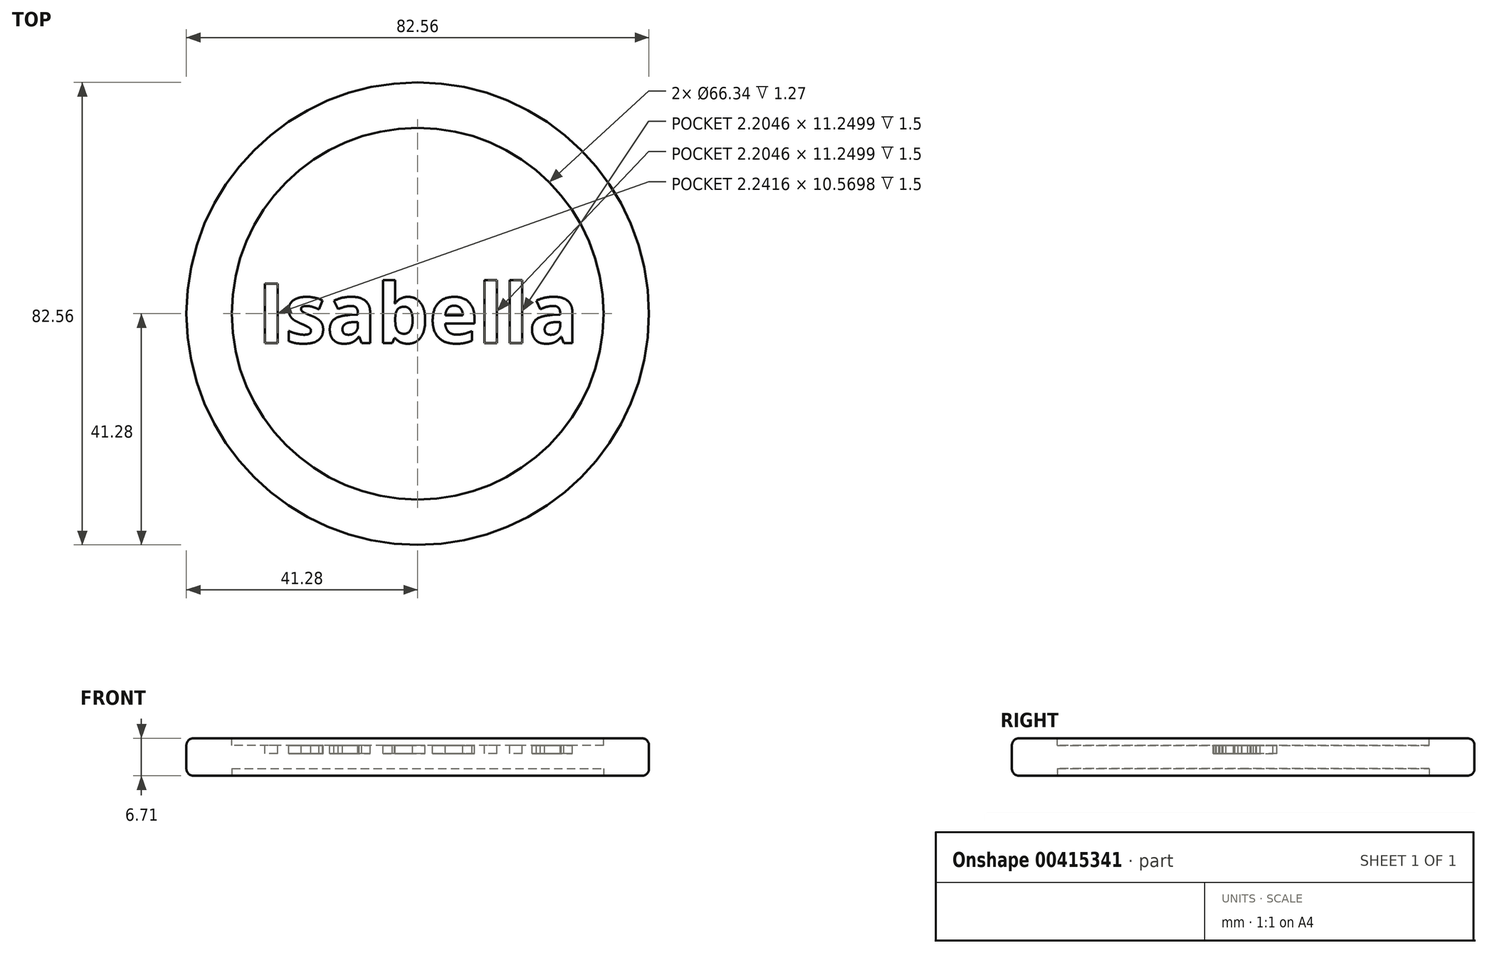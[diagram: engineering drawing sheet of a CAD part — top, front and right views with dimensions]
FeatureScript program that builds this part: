
annotation { "Feature Type Name" : "Feature", "Feature Type Description" : "" }
export const myFeature = defineFeature(function(context is Context, id is Id, definition is map)
    precondition{}
    {
        {
            var Q0;
            Q0=qCreatedBy(makeId("Top.planeOp"),FACE);
            var sketch = newSketch(context, id + "F0", { "sketchPlane" : qUnion([Q0])});
            skCircle(sketch, "E0", {"center": v(0, 0) * mm, "radius": 41.28 * mm});
            skSolve(sketch);
        }
        {
            var Q0;
            Q0=makeQuery(id+"F0.imprint","IMPRINT",FACE,{"disambiguationData":[TD([[makeQuery(id+"F0.imprint","IMPRINT",EDGE,{"derivedFrom":sQuery(id+"F0.wireOp",EDGE,"E0")}),1.0]])]});
            extrude(context, id + "F1", {"entities" : qUnion([Q0]), "depth" : 6.7 * mm});
        }
        {
            var Q0;
            Q0=makeQuery(id+"F1.opExtrude","CAP_FACE",FACE,{"disambiguationData":[OSD([sQuery(id+"F0.wireOp",EDGE,"E0")])],"isStart":false});
            var sketch = newSketch(context, id + "F2", { "sketchPlane" : qUnion([Q0])});
            skCircle(sketch, "E1.0", {"center": v(0, 0) * mm, "radius": 33.17 * mm});
            skSolve(sketch);
        }
        {
            var Q0;
            Q0=makeQuery(id+"F2.imprint","IMPRINT",FACE,{"disambiguationData":[TD([[makeQuery(id+"F2.imprint","IMPRINT",EDGE,{"derivedFrom":sQuery(id+"F2.wireOp",EDGE,"E1.0")}),1.0]])]});
            extrude(context, id + "F3", {"entities" : qUnion([Q0]), "operationType" : NewBodyOperationType.REMOVE, "oppositeDirection" : true, "depth" : 1.27 * mm});
        }
        {
            var Q0;
            Q0=makeQuery(id+"F1.opExtrude","CAP_EDGE",EDGE,{"disambiguationData":[OSD([sQuery(id+"F0.wireOp",EDGE,"E0")])],"isStart":false});
            var Q1;
            Q1=makeQuery(id+"F1.opExtrude","CAP_EDGE",EDGE,{"disambiguationData":[OSD([sQuery(id+"F0.wireOp",EDGE,"E0")])],"isStart":true});
            var Q2;
            Q2=makeQuery(id+"F3.boolean.opBoolean","COPY",EDGE,{"derivedFrom":makeQuery(id+"F3.opExtrude","CAP_EDGE",EDGE,{"disambiguationData":[OSD([sQuery(id+"F2.wireOp",EDGE,"E1.0")])],"isStart":true})});
            fillet(context, id + "F4", {"entities" : qUnion([Q0, Q1, Q2]), "radius" : 1.27 * mm, "tangentPropagation" : true, "allowEdgeOverflow" : false});
        }
        {
            var Q0;
            Q0=makeQuery(id+"F3.boolean.opBoolean","COPY",FACE,{"derivedFrom":makeQuery(id+"F3.opExtrude","CAP_FACE",FACE,{"disambiguationData":[OSD([sQuery(id+"F2.wireOp",EDGE,"E1.0")])],"isStart":false})});
            var sketch = newSketch(context, id + "F5", { "sketchPlane" : qUnion([Q0])});
            skText(sketch, "E2", { "text": "Isabella", "fontName": "OpenSans-Bold.ttf"});
            skLineSegment(sketch, "E3", {"start": v(2.43, -5.23) * mm, "end": v(2.43, -16.13) * mm, "construction": true});
            const initialGuessF5  = {"E2": [-0.02857, -0.00523, 1, 0, 0.01066]};
            skSetInitialGuess(sketch, initialGuessF5);
            skSolve(sketch);
        }
        {
            var Q0;
            Q0 = qSketchRegion(id + "F5", true);
            extrude(context, id + "F6", {"entities" : qUnion([Q0]), "operationType" : NewBodyOperationType.REMOVE, "oppositeDirection" : true, "depth" : 1.5 * mm});
        }
        {
            var Q0;
            Q0=makeQuery(id+"F1.opExtrude","CAP_FACE",FACE,{"disambiguationData":[OSD([sQuery(id+"F0.wireOp",EDGE,"E0")])],"isStart":true});
            var sketch = newSketch(context, id + "F7", { "sketchPlane" : qUnion([Q0])});
            skCircle(sketch, "E4.0", {"center": v(0, 0) * mm, "radius": 33.17 * mm});
            skSolve(sketch);
        }
        {
            var Q0;
            Q0=makeQuery(id+"F7.imprint","IMPRINT",FACE,{"disambiguationData":[TD([[makeQuery(id+"F7.imprint","IMPRINT",EDGE,{"derivedFrom":sQuery(id+"F7.wireOp",EDGE,"E4.0")}),1.0]])]});
            extrude(context, id + "F8", {"entities" : qUnion([Q0]), "operationType" : NewBodyOperationType.REMOVE, "oppositeDirection" : true, "depth" : 1.27 * mm});
        }
    });
